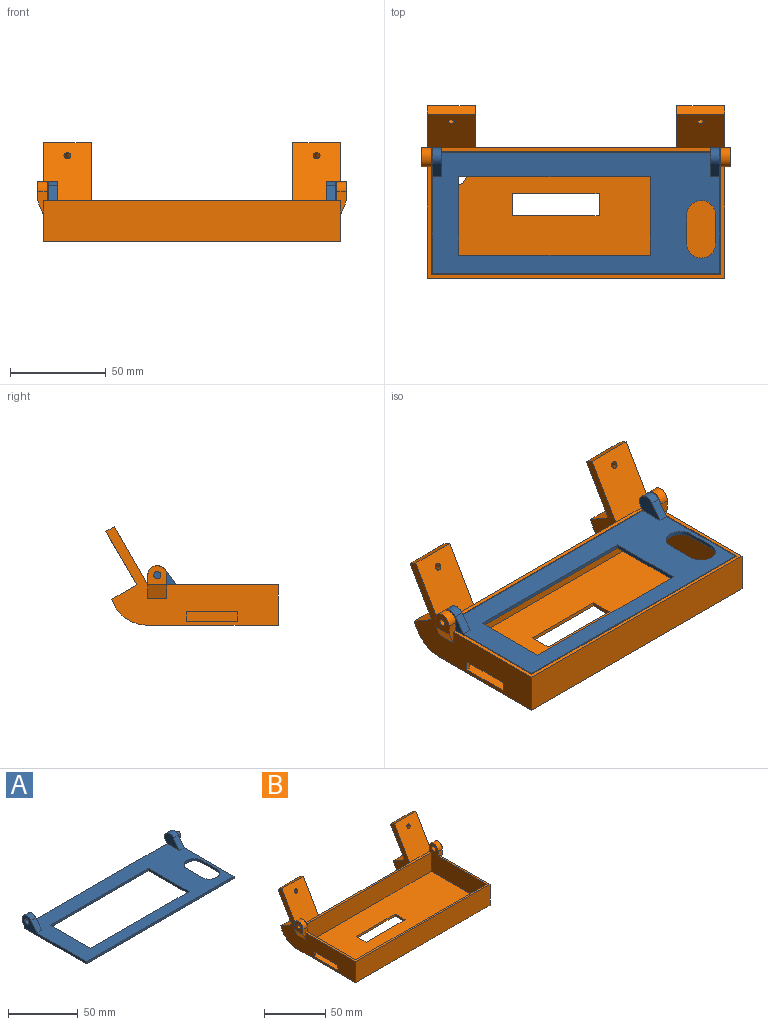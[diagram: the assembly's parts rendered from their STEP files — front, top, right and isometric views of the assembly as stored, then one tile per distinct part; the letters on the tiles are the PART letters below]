
ASSEMBLY  parts=2 mates=1
PART A: 25 faces, bbox 154x65.5x12 mm
  f0: plane 150x63mm, normal (0,0,1), area 4823.3mm2, adj f1,f2,f3,f4,f5,f6,f7,f8
  f1: plane 150x2mm, normal (0,1,0), area 300mm2, adj f0,f2,f12,f13,f15,f21
  f2: plane 65.5x12mm, normal (-1,0,0), area 213.9mm2, adj f0,f1,f3,f13,f20,f21,f22,f24
  f3: plane 150x2mm, normal (0,-1,0), area 300mm2, adj f0,f2,f12,f13
  f4: plane 41x2mm, normal (1,0,0), area 82mm2, adj f0,f5,f10,f13
  f5: plane 100x2mm, normal (0,-1,0), area 200mm2, adj f0,f4,f6,f13
  f6: plane 41x2mm, normal (-1,0,0), area 82mm2, adj f0,f5,f10,f13
  f7: plane 15x2mm, normal (1,0,0), area 30mm2, adj f0,f8,f11,f13
  f8: cylinder r=7.5mm len=15mm, axis (0,0,-1), area 47.1mm2, adj f0,f7,f9,f13
  f9: plane 15x2mm, normal (-1,0,0), area 30mm2, adj f0,f8,f11,f13
  f10: plane 100x2mm, normal (0,1,0), area 200mm2, adj f0,f4,f6,f13
  f11: cylinder r=7.5mm len=15mm, axis (0,0,-1), area 47.1mm2, adj f0,f7,f9,f13
  f12: plane 65.5x12mm, normal (1,0,0), area 209.7mm2, adj f0,f1,f3,f13,f14,f15,f16,f18
  f13: plane 150x63mm, normal (0,0,-1), area 4948.3mm2, adj f1,f2,f3,f4,f5,f6,f7,f8
  f14: plane 8x6mm, normal (0,-0.8,0.6), area 50mm2, adj f0,f12,f16,f17
  f15: plane 5x2mm, normal (0,0.8,-0.6), area 12.5mm2, adj f1,f12,f16,f17
  f16: cylinder r=5mm len=9mm, axis (1,0,0), area 78.5mm2, adj f12,f14,f15,f17
  f17: plane 15x10mm, normal (-1,0,0), area 101.8mm2, adj f0,f14,f15,f16
  f18: cylinder r=2.4mm len=4.8mm, axis (-1,0,0), area 60.3mm2, adj f12,f19
  f19: plane 4.8x4.8mm, normal (1,0,0), area 18.1mm2, adj f18
  f20: cylinder r=5mm len=9mm, axis (-1,0,0), area 78.5mm2, adj f2,f21,f22,f23
  f21: plane 5x2mm, normal (0,0.8,-0.6), area 12.5mm2, adj f1,f2,f20,f23
  f22: plane 8x6mm, normal (0,-0.8,0.6), area 50mm2, adj f0,f2,f20,f23
  f23: plane 15x10mm, normal (1,0,0), area 87.9mm2, adj f0,f20,f21,f22,f24
  f24: cylinder r=2.1mm len=5mm, axis (-1,0,0), area 66mm2, adj f2,f23
PART B: 60 faces, bbox 161x89.8x51.3 mm
  f0: plane 105x21mm, normal (0,1,0), area 2205mm2, adj f9,f18,f42,f47
  f1: plane 15x4.33mm, normal (0,0.87,-0.5), area 75mm2, adj f2,f46,f52,f57
  f2: plane 16.26x15mm, normal (0,-0.5,-0.87), area 281.7mm2, adj f1,f4,f52,f57
  f3: plane 18.56x15mm, normal (0,1,0), area 278.4mm2, adj f7,f18,f49,f54
  f4: plane 18.56x15mm, normal (0,1,0), area 278.4mm2, adj f2,f18,f52,f57
  f5: plane 12x5mm, normal (0,1,0), area 35.5mm2, adj f12,f14,f29,f31,f32,f38
  f6: plane 15x4.33mm, normal (0,0.87,-0.5), area 75mm2, adj f7,f41,f49,f54
  f7: plane 16.26x15mm, normal (0,-0.5,-0.87), area 281.7mm2, adj f3,f6,f49,f54
  f8: plane 12x5mm, normal (0,1,0), area 35.5mm2, adj f11,f16,f33,f35,f37,f43
  f9: plane 151x2mm, normal (0,0,1), area 302mm2, adj f0,f14,f15,f16,f38,f43
  f10: plane 155x58mm, normal (0,0,1), area 534mm2, adj f11,f12,f13,f14,f16,f17,f28,f34
  f11: plane 89.83x51.31mm, normal (1,0,0), area 1793.4mm2, adj f8,f10,f13,f18,f33,f34,f43,f44
  f12: plane 89.83x51.31mm, normal (-1,0,0), area 1668mm2, adj f5,f10,f13,f18,f24,f25,f26,f27
  f13: plane 155x21mm, normal (0,-1,0), area 3255mm2, adj f10,f11,f12,f18
  f14: plane 66x29mm, normal (1,0,0), area 1158.9mm2, adj f5,f9,f10,f15,f17,f24,f25,f26
  f15: plane 151x19mm, normal (0,-1,0), area 2869mm2, adj f9,f14,f16,f24
  f16: plane 66x29mm, normal (-1,0,0), area 1285.6mm2, adj f8,f9,f10,f15,f17,f24,f34,f35
  f17: plane 151x19mm, normal (0,1,0), area 2869mm2, adj f10,f14,f16,f24
  f18: plane 155x68mm, normal (0,0,-1), area 9951.6mm2, adj f0,f3,f4,f11,f12,f13,f19,f20
  f19: plane 11.5x2mm, normal (1,0,0), area 23mm2, adj f18,f20,f23,f24
  f20: plane 45x2mm, normal (0,-1,0), area 90mm2, adj f18,f19,f21,f24
  f21: plane 11.5x2mm, normal (-1,0,0), area 23mm2, adj f18,f20,f23,f24
  f22: cylinder r=4.75mm len=9.5mm, axis (0,0,-1), area 59.7mm2, adj f18,f24
  f23: plane 45x2mm, normal (0,1,0), area 90mm2, adj f18,f19,f21,f24
  f24: plane 153x64mm, normal (0,0,1), area 9129.6mm2, adj f12,f14,f15,f16,f17,f19,f20,f21
  f25: plane 27x2mm, normal (0,0,-1), area 54mm2, adj f12,f14,f26,f27
  f26: plane 5x2mm, normal (0,-1,0), area 10mm2, adj f12,f14,f24,f25
  f27: plane 5x2mm, normal (0,1,0), area 10mm2, adj f12,f14,f24,f25
  f28: plane 12x5mm, normal (0,-1,0), area 35.5mm2, adj f10,f12,f14,f29,f31,f32
  f29: cylinder r=5mm len=10mm, axis (1,0,0), area 78.5mm2, adj f5,f14,f28,f31
  f30: cylinder r=1.9mm len=5mm, axis (1,0,0), area 59.7mm2, adj f14,f31
  f31: plane 10x10mm, normal (-1,0,0), area 77.9mm2, adj f5,f28,f29,f30,f32
  f32: plane 10x7mm, normal (-0.92,0,-0.39), area 76.2mm2, adj f5,f12,f28,f31
  f33: plane 10x7mm, normal (0.92,0,-0.39), area 76.2mm2, adj f8,f11,f34,f37
  f34: plane 12x5mm, normal (0,-1,0), area 35.5mm2, adj f10,f11,f16,f33,f35,f37
  f35: cylinder r=5mm len=10mm, axis (-1,0,0), area 78.5mm2, adj f8,f16,f34,f37
  f36: cylinder r=2.5mm len=5mm, axis (-1,0,0), area 78.5mm2, adj f16,f37
  f37: plane 10x10mm, normal (1,0,0), area 69.6mm2, adj f8,f33,f34,f35,f36
  f38: plane 30.31x25mm, normal (0,-0.87,0.5), area 865.4mm2, adj f5,f9,f12,f39,f42,f59
  f39: plane 25x4.33mm, normal (0,0.5,0.87), area 125mm2, adj f12,f38,f40,f42
  f40: plane 27.81x25mm, normal (0,0.87,-0.5), area 793.2mm2, adj f12,f39,f41,f42,f59
  f41: plane 25x12.99mm, normal (0,0.5,0.87), area 375mm2, adj f6,f12,f40,f42,f48,f53
  f42: plane 51.31x21.83mm, normal (1,0,0), area 445mm2, adj f0,f38,f39,f40,f41,f53
  f43: plane 30.31x25mm, normal (0,-0.87,0.5), area 865.4mm2, adj f8,f9,f11,f44,f47,f58
  f44: plane 25x4.33mm, normal (0,0.5,0.87), area 125mm2, adj f11,f43,f45,f47
  f45: plane 27.81x25mm, normal (0,0.87,-0.5), area 793.2mm2, adj f11,f44,f46,f47,f58
  f46: plane 25x12.99mm, normal (0,0.5,0.87), area 375mm2, adj f1,f11,f45,f47,f50,f55
  f47: plane 51.31x21.83mm, normal (-1,0,0), area 406.6mm2, adj f0,f43,f44,f45,f46,f55,f56
  f48: cylinder r=19.79mm len=18.76mm, axis (-1,0,0), area 123.4mm2, adj f12,f18,f41,f49
  f49: plane 18.76x18.56mm, normal (1,0,0), area 185.8mm2, adj f3,f6,f7,f48
  f50: cylinder r=19.79mm len=18.76mm, axis (-1,0,0), area 123.4mm2, adj f11,f18,f46,f52
  f51: cylinder r=1.75mm len=5mm, axis (-1,0,0), area 55mm2, adj f11,f52
  f52: plane 18.76x18.56mm, normal (-1,0,0), area 176.1mm2, adj f1,f2,f4,f50,f51
  f53: cylinder r=19.79mm len=18.76mm, axis (-1,0,0), area 123.4mm2, adj f18,f41,f42,f54
  f54: plane 18.76x18.56mm, normal (-1,0,0), area 185.8mm2, adj f3,f6,f7,f53
  f55: cylinder r=19.79mm len=18.76mm, axis (-1,0,0), area 123.4mm2, adj f18,f46,f47,f57
  f56: cylinder r=3.5mm len=7mm, axis (-1,0,0), area 110mm2, adj f47,f57
  f57: plane 18.76x18.56mm, normal (1,0,0), area 147.3mm2, adj f1,f2,f4,f55,f56
  f58: cylinder r=1.75mm len=6.08mm, axis (0,-0.87,0.5), area 55mm2, adj f43,f45
  f59: cylinder r=1.75mm len=6.08mm, axis (0,-0.87,0.5), area 55mm2, adj f38,f40
PLACE A t=(-8.03,16.9,35.81)mm
PLACE B t=(-8.03,16.9,16.81)mm
MATE revolute B.f29 <-> A.f20  axis (-1,0,0) through (67.47,45.9,42.81)mm
